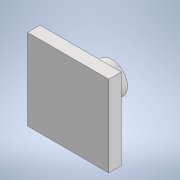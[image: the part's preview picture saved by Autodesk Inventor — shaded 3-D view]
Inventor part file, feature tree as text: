
AUTODESK INVENTOR PART (.ipt)
format: ipt  version: 2022 (Build 260153000, 153)  size: 96,768 bytes
history: native  units: mm
features: extrude x2, sketch x1
ambient origin geometry x8: Origin, YZ Plane, XZ Plane, XY Plane, X Axis, Y Axis, Z Axis, Center Point
bodies: Solid1 (feature_tree)
feature tree (3):
  sketch  "Sketch1"  dims[d0=5.0mm d1=26.0mm d2=26.0mm d3=10.0mm d4=0.0mm d5=4.0mm d6=0.0mm]
  extrude  "Extrusion1"  Depth=26.0mm
  extrude  "Extrusion2"  Depth=26.0mm
